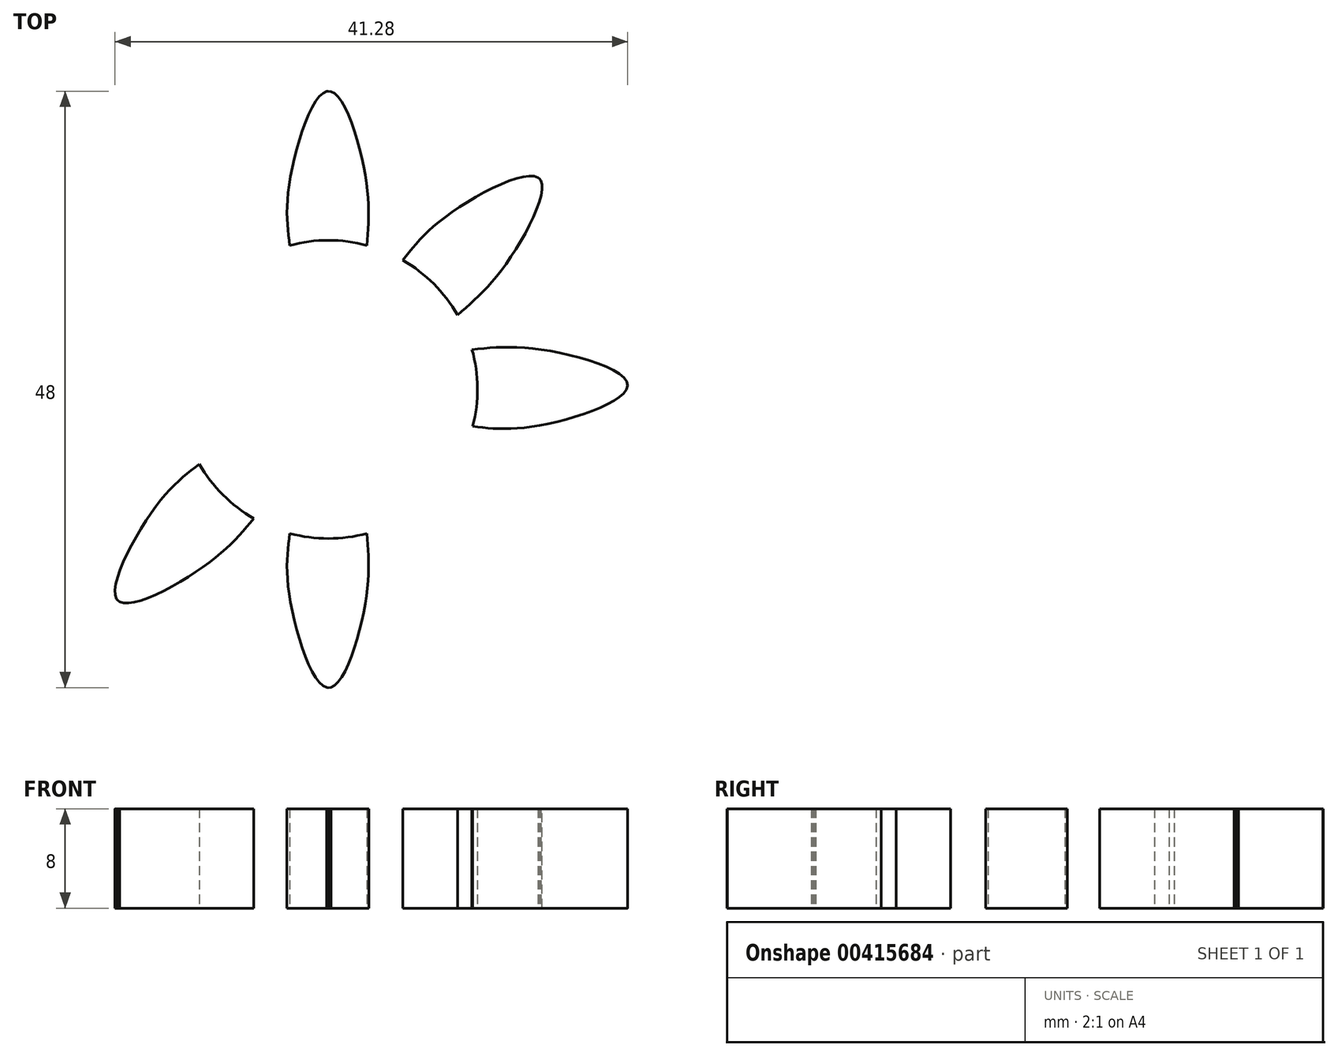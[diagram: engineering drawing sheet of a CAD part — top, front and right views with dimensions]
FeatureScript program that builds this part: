
annotation { "Feature Type Name" : "Feature", "Feature Type Description" : "" }
export const myFeature = defineFeature(function(context is Context, id is Id, definition is map)
    precondition{}
    {
        {
            var Q0;
            Q0=qCreatedBy(makeId("Top.planeOp"),FACE);
            var sketch = newSketch(context, id + "F0", { "sketchPlane" : qUnion([Q0])});
            skCircle(sketch, "E0", {"center": v(0, 0) * mm, "radius": 12 * mm});
            skCircle(sketch, "E1.cCircle", {"center": v(0, 0) * mm, "radius": 12 * mm, "construction": true});
            skLineSegment(sketch, "E2.0", {"start": v(0, 24) * mm, "end": v(0.2, 23.97) * mm});
            skLineSegment(sketch, "E2.2", {"start": v(16.87, 17.05) * mm, "end": v(16.97, 16.97) * mm});
            skLineSegment(sketch, "E2.3", {"start": v(16.97, 16.97) * mm, "end": v(17.1, 16.81) * mm});
            skLineSegment(sketch, "E2.6", {"start": v(24, 0) * mm, "end": v(24, -0.02) * mm});
            skLineSegment(sketch, "E2.11", {"start": v(0.2, -23.97) * mm, "end": v(0, -24) * mm});
            skLineSegment(sketch, "E2.12", {"start": v(0, -24) * mm, "end": v(-0.12, -23.98) * mm});
            skLineSegment(sketch, "E2.14", {"start": v(-16.81, -17.1) * mm, "end": v(-16.97, -16.97) * mm});
            skLineSegment(sketch, "E2.15", {"start": v(-16.97, -16.97) * mm, "end": v(-17.05, -16.87) * mm});
            skLineSegment(sketch, "E2.23", {"start": v(-0.12, 23.98) * mm, "end": v(0, 24) * mm});
            skFitSpline(sketch, "E3", {"points": [v(-3.1, 11.6) * mm, v(-3.1, 16.81) * mm, v(0, 24) * mm, v(2.96, 17.34) * mm, v(3.1, 11.6) * mm], "startDerivative": vector(-2.57, 19.16) * mm, "endDerivative": vector(-1.8, -20.76) * mm});
            skLineSegment(sketch, "E4.7.1", {"start": v(24, 0) * mm, "end": v(24, 0) * mm});
            skArc(sketch, "E5.2.0", {"start": v(-10.14, 6.41) * mm, "mid": v(-11.05, 4.68) * mm, "end": v(-11.67, 2.81) * mm, "construction": true});
            skFitSpline(sketch, "E6.MirrorCS", {"points": [v(-3.1, -11.6) * mm, v(-3.1, -16.81) * mm, v(0, -24) * mm, v(2.96, -17.34) * mm, v(3.1, -11.6) * mm], "startDerivative": vector(-2.57, -19.16) * mm, "endDerivative": vector(-1.8, 20.76) * mm});
            skFitSpline(sketch, "E7.MirrorCS", {"points": [v(11.62, -2.98) * mm, v(16.97, -2.9) * mm, v(24.1, 0.33) * mm, v(17.39, 3.17) * mm, v(11.56, 3.21) * mm], "startDerivative": vector(19.2, -2.23) * mm, "endDerivative": vector(-20.72, -2.17) * mm});
            skFitSpline(sketch, "E8.MirrorCS", {"points": [v(-11.43, -3.41) * mm, v(-16.65, -3.5) * mm, v(-23.9, -0.53) * mm, v(-17.3, 2.55) * mm, v(-11.67, 2.81) * mm], "startDerivative": vector(-19.1, -2.91) * mm, "endDerivative": vector(20.79, -1.43) * mm});
            skFitSpline(sketch, "E9.MirrorCS", {"points": [v(-11.43, -3.41) * mm, v(-16.65, -3.5) * mm, v(-23.9, -0.53) * mm, v(-17.3, 2.55) * mm, v(-11.67, 2.81) * mm], "startDerivative": vector(-19.1, -2.91) * mm, "endDerivative": vector(20.79, -1.43) * mm});
            skFitSpline(sketch, "E10.MirrorCS", {"points": [v(-5.67, 10.5) * mm, v(-9.3, 14.25) * mm, v(-16.52, 17.27) * mm, v(-14.03, 10.43) * mm, v(-10.24, 6.26) * mm], "startDerivative": vector(-11.45, 15.57) * mm, "endDerivative": vector(15.71, -13.69) * mm});
            skFitSpline(sketch, "E11.MirrorCS", {"points": [v(10.29, -6.18) * mm, v(14.05, -9.94) * mm, v(16.8, -17.27) * mm, v(10.06, -14.53) * mm, v(5.9, -10.44) * mm], "startDerivative": vector(15.15, -12) * mm, "endDerivative": vector(-13.12, 16.19) * mm});
            skFitSpline(sketch, "E12.MirrorCS", {"points": [v(10.29, -6.18) * mm, v(14.05, -9.94) * mm, v(16.8, -17.27) * mm, v(10.06, -14.53) * mm, v(5.95, -10.5) * mm], "startDerivative": vector(15.15, -12) * mm, "endDerivative": vector(-13.12, 16.19) * mm});
            skFitSpline(sketch, "E13.MirrorCS", {"points": [v(-10.4, -6) * mm, v(-14.08, -9.7) * mm, v(-16.97, -16.97) * mm, v(-10.17, -14.35) * mm, v(-6, -10.4) * mm], "startDerivative": vector(-15.36, -11.73) * mm, "endDerivative": vector(13.4, 15.95) * mm});
            skFitSpline(sketch, "E14.MirrorCS", {"points": [v(6, 10.4) * mm, v(9.7, 14.08) * mm, v(16.97, 16.97) * mm, v(14.35, 10.17) * mm, v(10.4, 6) * mm], "startDerivative": vector(11.73, 15.36) * mm, "endDerivative": vector(-15.95, -13.4) * mm});
            skArc(sketch, "E15", {"start": v(-11.67, 2.81) * mm, "mid": v(12, 0.31) * mm, "end": v(-11.5, -3.42) * mm, "construction": true});
            skArc(sketch, "E16.trimOffspring", {"start": v(-11.5, -3.42) * mm, "mid": v(11.63, -2.95) * mm, "end": v(-8.49, 8.49) * mm, "construction": true});
            skSolve(sketch);
        }
        {
            var Q0;
            {var subQ0=sQuery(id+"F0.wireOp",EDGE,"E0");var subQ12=sQuery(id+"F0.wireOp",EDGE,"E6.MirrorCS");var subQ13=makeQuery(id+"F0.imprint","INTERSECT",VERTEX,{"disambiguationData":[OD(1.0)],"derivedFrom":[subQ12,subQ0]});Q0=makeQuery(id+"F0.imprint","IMPRINT",FACE,{"disambiguationData":[TD([[makeQuery(id+"F0.imprint","IMPRINT",EDGE,{"disambiguationData":[TD([[subQ13,1.0]])],"derivedFrom":subQ0}),-1.0]])]});}
            var Q1;
            {var subQ0=sQuery(id+"F0.wireOp",EDGE,"E9.MirrorCS");Q1=makeQuery(id+"F0.imprint","IMPRINT",FACE,{"disambiguationData":[TD([[makeQuery(id+"F0.imprint","IMPRINT",EDGE,{"derivedFrom":subQ0}),-1.0]])]});}
            var Q2;
            {var subQ0=sQuery(id+"F0.wireOp",EDGE,"E10.MirrorCS");var subQ1=sQuery(id+"F0.wireOp",EDGE,"E0");var subQ2=makeQuery(id+"F0.imprint","INTERSECT",VERTEX,{"disambiguationData":[OD(0.0)],"derivedFrom":[subQ1,subQ0]});Q2=makeQuery(id+"F0.imprint","IMPRINT",FACE,{"disambiguationData":[TD([[makeQuery(id+"F0.imprint","IMPRINT",EDGE,{"disambiguationData":[TD([[subQ2,-1.0]])],"derivedFrom":subQ1}),1.0]])]});}
            var Q3;
            {var subQ2=sQuery(id+"F0.wireOp",EDGE,"E2.0");Q3=makeQuery(id+"F0.imprint","IMPRINT",FACE,{"disambiguationData":[TD([[makeQuery(id+"F0.imprint","IMPRINT",EDGE,{"derivedFrom":subQ2}),-1.0]])]});}
            var Q4;
            {var subQ1=sQuery(id+"F0.wireOp",EDGE,"E2.2");Q4=makeQuery(id+"F0.imprint","IMPRINT",FACE,{"disambiguationData":[TD([[makeQuery(id+"F0.imprint","IMPRINT",EDGE,{"derivedFrom":subQ1}),-1.0]])]});}
            var Q5;
            {var subQ0=sQuery(id+"F0.wireOp",EDGE,"E7.MirrorCS");var subQ1=makeQuery(id+"F0.imprint","IMPRINT",VERTEX,{"derivedFrom":subQ0});Q5=makeQuery(id+"F0.imprint","IMPRINT",FACE,{"disambiguationData":[TD([[makeQuery(id+"F0.imprint","IMPRINT",EDGE,{"disambiguationData":[TD([[subQ1,1.0]])],"derivedFrom":subQ0}),1.0]])]});}
            var Q6;
            {var subQ1=sQuery(id+"F0.wireOp",EDGE,"E11.MirrorCS");var subQ6=sQuery(id+"F0.wireOp",EDGE,"E0");var subQ7=makeQuery(id+"F0.imprint","INTERSECT",VERTEX,{"derivedFrom":[subQ6,subQ1]});Q6=makeQuery(id+"F0.imprint","IMPRINT",FACE,{"disambiguationData":[TD([[makeQuery(id+"F0.imprint","IMPRINT",EDGE,{"disambiguationData":[TD([[subQ7,1.0]])],"derivedFrom":subQ6}),1.0]])]});}
            var Q7;
            {var subQ4=sQuery(id+"F0.wireOp",EDGE,"E2.12");Q7=makeQuery(id+"F0.imprint","IMPRINT",FACE,{"disambiguationData":[TD([[makeQuery(id+"F0.imprint","IMPRINT",EDGE,{"derivedFrom":subQ4}),-1.0]])]});}
            var Q8;
            {var subQ5=sQuery(id+"F0.wireOp",EDGE,"E2.15");Q8=makeQuery(id+"F0.imprint","IMPRINT",FACE,{"disambiguationData":[TD([[makeQuery(id+"F0.imprint","IMPRINT",EDGE,{"derivedFrom":subQ5}),-1.0]])]});}
            extrude(context, id + "F1", {"entities" : qUnion([Q0, Q1, Q2, Q3, Q4, Q5, Q6, Q7, Q8]), "depth" : 8 * mm});
        }
        {
            var Q0;
            Q0=qCreatedBy(makeId("Top.planeOp"),FACE);
            var sketch = newSketch(context, id + "F2", { "sketchPlane" : qUnion([Q0])});
            skCircle(sketch, "E17", {"center": v(0, 0) * mm, "radius": 3.2 * mm});
            skSolve(sketch);
        }
        {
            var Q0;
            Q0 = qSketchRegion(id + "F2", true);
            extrude(context, id + "F3", {"entities" : qUnion([Q0]), "operationType" : NewBodyOperationType.REMOVE, "depth" : 8 * mm});
        }
    });
